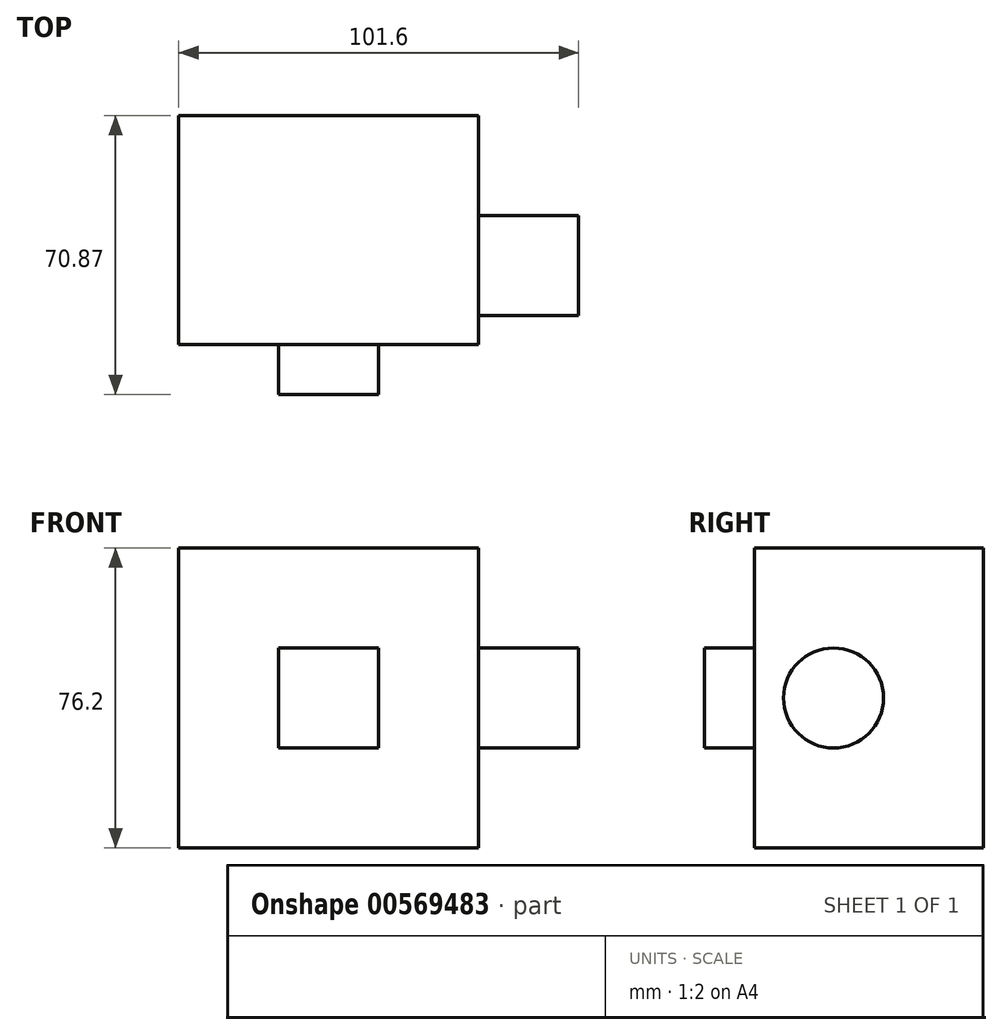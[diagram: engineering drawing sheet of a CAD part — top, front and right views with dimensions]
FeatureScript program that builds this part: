
annotation { "Feature Type Name" : "Feature", "Feature Type Description" : "" }
export const myFeature = defineFeature(function(context is Context, id is Id, definition is map)
    precondition{}
    {
        {
            var Q0;
            Q0=qCreatedBy(makeId("Front.planeOp"),FACE);
            var sketch = newSketch(context, id + "F0", { "sketchPlane" : qUnion([Q0])});
            skLineSegment(sketch, "E0.bottom", {"start": v(-128, 111.2) * mm, "end": v(-51.8, 111.2) * mm});
            skLineSegment(sketch, "E0.top", {"start": v(-128, 35) * mm, "end": v(-51.8, 35) * mm});
            skLineSegment(sketch, "E0.left", {"start": v(-128, 111.2) * mm, "end": v(-128, 35) * mm});
            skLineSegment(sketch, "E0.right", {"start": v(-51.8, 111.2) * mm, "end": v(-51.8, 35) * mm});
            skSolve(sketch);
        }
        {
            var Q0;
            Q0=makeQuery(id+"F0.imprint","IMPRINT",FACE,{"disambiguationData":[TD([[makeQuery(id+"F0.imprint","IMPRINT",EDGE,{"derivedFrom":sQuery(id+"F0.wireOp",EDGE,"E0.bottom")}),-1.0]])]});
            extrude(context, id + "F1", {"entities" : qUnion([Q0]), "depth" : 25.4 * mm, "offsetDistance" : 25.4 * mm});
        }
        {
            var Q0;
            Q0=makeQuery(id+"F1.opExtrude","CAP_FACE",FACE,{"disambiguationData":[OSD([sQuery(id+"F0.wireOp",EDGE,"E0.bottom"),sQuery(id+"F0.wireOp",EDGE,"E0.top"),sQuery(id+"F0.wireOp",EDGE,"E0.left"),sQuery(id+"F0.wireOp",EDGE,"E0.right")])],"isStart":false});
            extrude(context, id + "F2", {"entities" : qUnion([Q0]), "operationType" : NewBodyOperationType.ADD, "depth" : 32.77 * mm, "offsetDistance" : 25.4 * mm});
        }
        {
            var Q0;
            Q0=makeQuery(id+"F2.opExtrude","CAP_FACE",FACE,{"disambiguationData":[OSD([sQuery(id+"F0.wireOp",EDGE,"E0.bottom"),sQuery(id+"F0.wireOp",EDGE,"E0.top"),sQuery(id+"F0.wireOp",EDGE,"E0.left"),sQuery(id+"F0.wireOp",EDGE,"E0.right")])],"isStart":false});
            var sketch = newSketch(context, id + "F3", { "sketchPlane" : qUnion([Q0])});
            skLineSegment(sketch, "E1.bottom", {"start": v(-102.6, 85.8) * mm, "end": v(-77.2, 85.8) * mm});
            skLineSegment(sketch, "E1.top", {"start": v(-102.6, 60.4) * mm, "end": v(-77.2, 60.4) * mm});
            skLineSegment(sketch, "E1.left", {"start": v(-102.6, 85.8) * mm, "end": v(-102.6, 60.4) * mm});
            skLineSegment(sketch, "E1.right", {"start": v(-77.2, 85.8) * mm, "end": v(-77.2, 60.4) * mm});
            skSolve(sketch);
        }
        {
            var Q0;
            Q0=makeQuery(id+"F3.imprint","IMPRINT",FACE,{"disambiguationData":[TD([[makeQuery(id+"F3.imprint","IMPRINT",EDGE,{"derivedFrom":sQuery(id+"F3.wireOp",EDGE,"E1.bottom")}),-1.0]])]});
            extrude(context, id + "F4", {"entities" : qUnion([Q0]), "operationType" : NewBodyOperationType.ADD, "depth" : 12.7 * mm, "offsetDistance" : 25.4 * mm});
        }
        {
            var Q0;
            {var subQ0=sQuery(id+"F0.wireOp",EDGE,"E0.right");Q0=makeQuery(id+"F2.boolean.opBoolean","MERGE",FACE,{"derivedFrom":[makeQuery(id+"F1.opExtrude","SWEPT_FACE",FACE,{"disambiguationData":[OSD([subQ0])]}),makeQuery(id+"F2.opExtrude","SWEPT_FACE",FACE,{"disambiguationData":[OSD([subQ0])]})]});}
            var sketch = newSketch(context, id + "F5", { "sketchPlane" : qUnion([Q0])});
            skCircle(sketch, "E2", {"center": v(-38.1, 73.1) * mm, "radius": 12.7 * mm});
            skSolve(sketch);
        }
        {
            var Q0;
            Q0=makeQuery(id+"F5.imprint","IMPRINT",FACE,{"disambiguationData":[TD([[makeQuery(id+"F5.imprint","IMPRINT",EDGE,{"derivedFrom":sQuery(id+"F5.wireOp",EDGE,"E2")}),1.0]])]});
            var sketch = newSketch(context, id + "F6", { "sketchPlane" : qUnion([Q0])});
            skSolve(sketch);
        }
        {
            var Q0;
            Q0 = qSketchRegion(id + "F6", true);
            var Q1;
            Q1=makeQuery(id+"F5.imprint","IMPRINT",FACE,{"disambiguationData":[TD([[makeQuery(id+"F5.imprint","IMPRINT",EDGE,{"derivedFrom":sQuery(id+"F5.wireOp",EDGE,"E2")}),1.0]])]});
            extrude(context, id + "F7", {"entities" : qUnion([Q0, Q1]), "operationType" : NewBodyOperationType.ADD, "depth" : 25.4 * mm, "offsetDistance" : 25.4 * mm});
        }
    });
